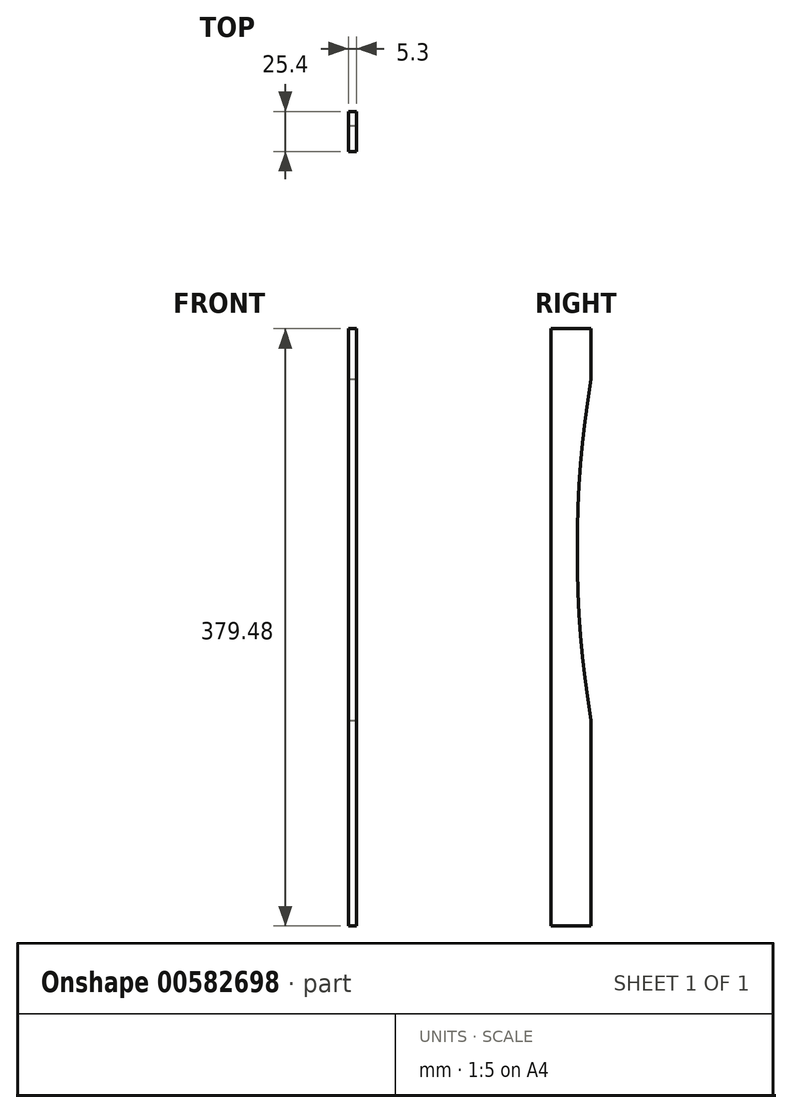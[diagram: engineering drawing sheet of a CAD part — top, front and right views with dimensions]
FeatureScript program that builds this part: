
annotation { "Feature Type Name" : "Feature", "Feature Type Description" : "" }
export const myFeature = defineFeature(function(context is Context, id is Id, definition is map)
    precondition{}
    {
        {
            var Q0;
            Q0=qCreatedBy(makeId("Front.planeOp"),FACE);
            var sketch = newSketch(context, id + "F0", { "sketchPlane" : qUnion([Q0])});
            skLineSegment(sketch, "E0", {"start": v(-47.14, 112.92) * mm, "end": v(-47.14, -266.56) * mm});
            skLineSegment(sketch, "E1", {"start": v(-47.14, -266.56) * mm, "end": v(-41.84, -266.56) * mm});
            skLineSegment(sketch, "E2", {"start": v(-41.84, -266.56) * mm, "end": v(-41.84, 112.92) * mm});
            skLineSegment(sketch, "E3", {"start": v(-41.84, 112.92) * mm, "end": v(-47.14, 112.92) * mm});
            skSolve(sketch);
        }
        {
            var Q0;
            Q0 = qSketchRegion(id + "F0", true);
            extrude(context, id + "F1", {"entities" : qUnion([Q0]), "depth" : 25.4 * mm, "offsetDistance" : 25.4 * mm});
        }
        {
            var Q0;
            Q0=makeQuery(id+"F1.opExtrude","SWEPT_FACE",FACE,{"disambiguationData":[OSD([sQuery(id+"F0.wireOp",EDGE,"E2")])]});
            var sketch = newSketch(context, id + "F2", { "sketchPlane" : qUnion([Q0])});
            skPoint(sketch, "E4", {"position": v(0, 80.96) * mm});
            skPoint(sketch, "E5", {"position": v(0, -136.04) * mm});
            skArc(sketch, "E6", {"start": v(0, 80.96) * mm, "mid": v(-8.8, -27.54) * mm, "end": v(0, -136.04) * mm});
            skLineSegment(sketch, "E7", {"start": v(0, 80.96) * mm, "end": v(0, -136.04) * mm});
            skSolve(sketch);
        }
        {
            var Q0;
            Q0 = qSketchRegion(id + "F2", true);
            extrude(context, id + "F3", {"entities" : qUnion([Q0]), "operationType" : NewBodyOperationType.REMOVE, "oppositeDirection" : true, "depth" : 25.4 * mm, "offsetDistance" : 25.4 * mm});
        }
    });
